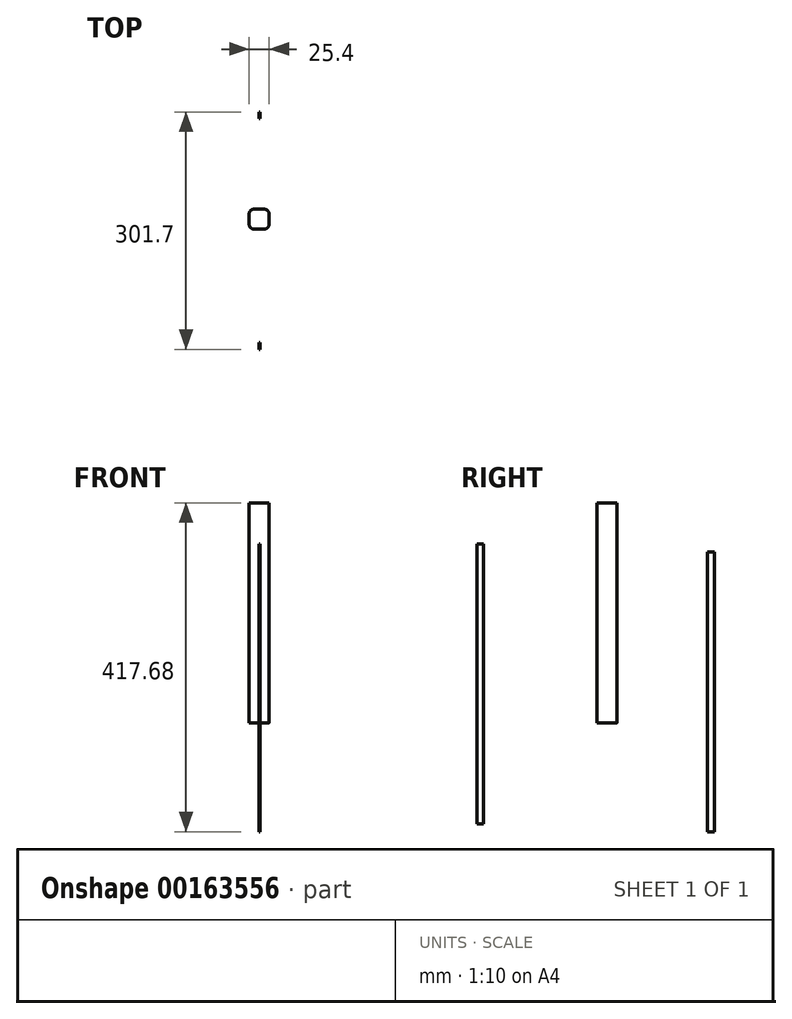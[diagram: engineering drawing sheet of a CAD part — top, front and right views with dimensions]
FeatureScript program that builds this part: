
annotation { "Feature Type Name" : "Feature", "Feature Type Description" : "" }
export const myFeature = defineFeature(function(context is Context, id is Id, definition is map)
    precondition{}
    {
        {
            var Q0;
            Q0=qCreatedBy(makeId("Top.planeOp"),FACE);
            var sketch = newSketch(context, id + "F0", { "sketchPlane" : qUnion([Q0])});
            skLineSegment(sketch, "E0.bottom", {"start": v(6.35, 12.7) * mm, "end": v(-6.35, 12.7) * mm});
            skLineSegment(sketch, "E0.top", {"start": v(6.35, -12.7) * mm, "end": v(-6.35, -12.7) * mm});
            skLineSegment(sketch, "E0.left", {"start": v(12.7, 6.35) * mm, "end": v(12.7, -6.35) * mm});
            skLineSegment(sketch, "E0.right", {"start": v(-12.7, 6.35) * mm, "end": v(-12.7, -6.35) * mm});
            skPoint(sketch, "E0.middle", {"position": v(0, 0) * mm});
            skPoint(sketch, "E1.visualSharp", {"position": v(-12.7, 12.7) * mm});
            skArc(sketch, "E1.filletArc", {"start": v(-6.35, 12.7) * mm, "mid": v(-10.84, 10.84) * mm, "end": v(-12.7, 6.35) * mm});
            skPoint(sketch, "E2.visualSharp", {"position": v(-12.7, -12.7) * mm});
            skArc(sketch, "E2.filletArc", {"start": v(-12.7, -6.35) * mm, "mid": v(-10.84, -10.84) * mm, "end": v(-6.35, -12.7) * mm});
            skPoint(sketch, "E3.visualSharp", {"position": v(12.7, -12.7) * mm});
            skArc(sketch, "E3.filletArc", {"start": v(6.35, -12.7) * mm, "mid": v(10.84, -10.84) * mm, "end": v(12.7, -6.35) * mm});
            skPoint(sketch, "E4.visualSharp", {"position": v(12.7, 12.7) * mm});
            skArc(sketch, "E4.filletArc", {"start": v(12.7, 6.35) * mm, "mid": v(10.84, 10.84) * mm, "end": v(6.35, 12.7) * mm});
            skSolve(sketch);
        }
        {
            var Q0;
            Q0=qSketchRegion(id+"F0",true);
            extrude(context, id + "F1", {"entities" : qUnion([Q0]), "depth" : 279.4 * mm});
        }
        {
            var Q0;
            Q0=qCreatedBy(makeId("Right.planeOp"),FACE);
            var sketch = newSketch(context, id + "F2", { "sketchPlane" : qUnion([Q0])});
            skLineSegment(sketch, "E5.bottom", {"start": v(-165.43, 227.1) * mm, "end": v(-156.96, 227.1) * mm});
            skLineSegment(sketch, "E5.top", {"start": v(-165.43, -128.5) * mm, "end": v(-156.96, -128.5) * mm});
            skLineSegment(sketch, "E5.left", {"start": v(-165.43, 227.1) * mm, "end": v(-165.43, -128.5) * mm});
            skLineSegment(sketch, "E5.right", {"start": v(-156.96, 227.1) * mm, "end": v(-156.96, -128.5) * mm});
            skSolve(sketch);
        }
        {
            var Q0;
            Q0=qSketchRegion(id+"F2",true);
            extrude(context, id + "F3", {"entities" : qUnion([Q0]), "depth" : 1.27 * mm});
        }
        {
            var Q0;
            Q0=qCreatedBy(makeId("Right.planeOp"),FACE);
            var sketch = newSketch(context, id + "F4", { "sketchPlane" : qUnion([Q0])});
            skLineSegment(sketch, "E6.bottom", {"start": v(127.8, 217.32) * mm, "end": v(136.27, 217.32) * mm});
            skLineSegment(sketch, "E6.top", {"start": v(127.8, -138.28) * mm, "end": v(136.27, -138.28) * mm});
            skLineSegment(sketch, "E6.left", {"start": v(127.8, 217.32) * mm, "end": v(127.8, -138.28) * mm});
            skLineSegment(sketch, "E6.right", {"start": v(136.27, 217.32) * mm, "end": v(136.27, -138.28) * mm});
            skSolve(sketch);
        }
        {
            var Q0;
            Q0=qSketchRegion(id+"F4",true);
            extrude(context, id + "F5", {"entities" : qUnion([Q0]), "depth" : 1.27 * mm});
        }
    });
